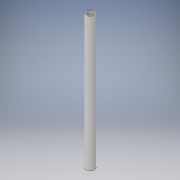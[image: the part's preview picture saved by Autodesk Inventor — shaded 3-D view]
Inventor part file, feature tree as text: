
AUTODESK INVENTOR PART (.ipt)
format: ipt  version: 2019 (Build 230136000, 136)  size: 123,392 bytes
history: native  units: in
note: dims shown in document units (in); Inventor stores cm internally (conversion verified against a paired STEP export)
features: extrude x4, sketch x4, plane x1
ambient origin geometry x8: Origin, YZ Plane, XZ Plane, XY Plane, X Axis, Y Axis, Z Axis, Center Point
bodies: Solid1 (feature_tree)
feature tree (9):
  extrude  "Extrusion1"  Depth=0.76in
  extrude  "Extrusion2"  Depth=7.875in TaperAngle=0.0deg
  extrude  "Extrusion3"  Depth=0.125in
  plane  "Work Plane2"
  extrude  "Extrusion5"  Depth=0.125in TaperAngle=0.0deg
  sketch  "Sketch1"  dims[d0=1.0in d1=0.76in]
  sketch  "Sketch2"  dims[d2=16.0in d3=0.0in d8=7.875in d9=0.0in]
  sketch  "Sketch3"  dims[d10=0.25in d11=0.0in d14=0.125in]
  sketch  "Sketch7"  dims[d15=0.125in d16=0.125in d17=0.0in]
